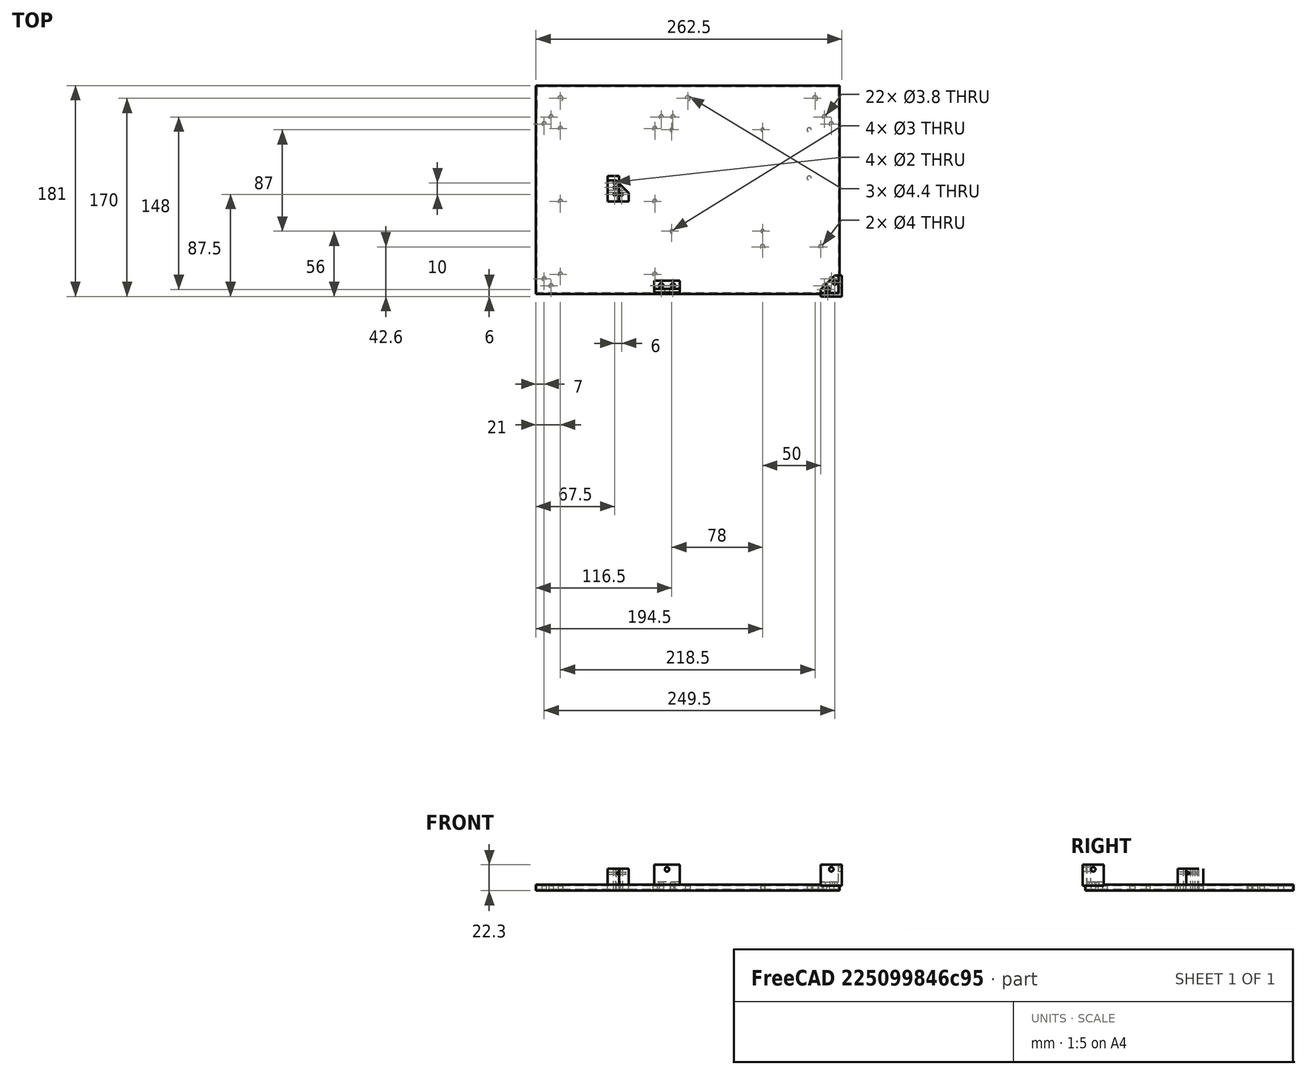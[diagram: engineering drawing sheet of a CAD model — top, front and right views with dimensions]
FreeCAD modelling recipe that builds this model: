
FCSTD DOCUMENT  (FreeCAD 0.18.4R)
Label: bottom_plate
License: All rights reserved
LicenseURL: http://en.wikipedia.org/wiki/All_rights_reserved
objects: Path::FeaturePython×8, Sketcher::SketchObject×6, PartDesign::Pad×6, PartDesign::Body×5, Part::Cylinder×5, Mesh::Feature×4, Part::Part2DObjectPython×4, Part::FeaturePython×4, Part::Box×3, PartDesign::FeatureBase×2, Part::MultiFuse×2, Part::Cut×2, App::Part×2, Spreadsheet::Sheet×1, App::FeaturePython×1, App::DocumentObjectGroup×1, Path::FeatureCompoundPython×1
note: 47 computed .brp shape members not serialized (recipe doc carries the construction recipe); baked Part::Feature solids carry a one-line shape summary decoded from their .brp

FEATURE [Sketcher::SketchObject] Sketch
  MapMode = 5
  Support = -> [XY_Plane]
  expr: Constraints[69] = p.bracket_hole_edge_dist
  expr: Constraints[20] = p.cisco_hole_dist_x
  expr: Constraints[63] = p.bracket_hole_edge_dist
  expr: Constraints[66] = p.bracket_hole_edge_dist
  expr: Constraints[21] = p.cisco_hole_dist_y / 2
  expr: Constraints[51] = p.bracket_hole_edge_dist
  expr: Constraints[54] = p.bracket_hole_dist
  expr: Constraints[13] = p.cisco_hole_dist_y
  expr: Constraints[78] = p.bracket_hole
  expr: Constraints[74] = p.bracket_hole_edge_dist
  expr: Constraints[67] = p.bracket_hole_edge_dist
  expr: Constraints[80] = p.bracket_hole_edge_dist
  expr: Constraints[19] = p.cisco_hole_dist_x
  expr: Constraints[50] = p.bracket_hole_edge_dist
  expr: Constraints[68] = p.bracket_hole_edge_dist
  expr: Constraints[73] = p.bracket_hole_edge_dist
  expr: Constraints[84] = p.bracket_hole_dist
  expr: Constraints[76] = p.bracket_hole_edge_dist
  expr: Constraints[64] = p.bracket_hole_edge_dist
  expr: Constraints[72] = p.bracket_hole_edge_dist
  expr: Constraints[75] = p.bracket_hole_edge_dist
  sketch-geometry (35):
    g0: LineSegment StartX=-78.5 StartY=198 StartZ=0 EndX=78.5 EndY=198 EndZ=0
    g1: LineSegment StartX=78.5 StartY=198 StartZ=0 EndX=78.5 EndY=-60.5 EndZ=0
    g2: LineSegment StartX=78.5 StartY=-60.5 StartZ=0 EndX=-78.5 EndY=-60.5 EndZ=0
    g3: Circle CenterX=-62.5 CenterY=-40.5 CenterZ=0 NormalX=0 NormalY=0 NormalZ=1 AngleXU=0 Radius=1.9
    g4: Circle CenterX=0 CenterY=-40.5 CenterZ=0 NormalX=0 NormalY=0 NormalZ=1 AngleXU=0 Radius=1.9
    g5: Circle CenterX=62.5 CenterY=-40.5 CenterZ=0 NormalX=0 NormalY=0 NormalZ=1 AngleXU=0 Radius=1.9
    g6: Circle CenterX=-62.5 CenterY=40.5 CenterZ=0 NormalX=0 NormalY=0 NormalZ=1 AngleXU=0 Radius=1.9
    g7: Circle CenterX=0 CenterY=40.5 CenterZ=0 NormalX=0 NormalY=0 NormalZ=1 AngleXU=0 Radius=1.9
    g8: Circle CenterX=62.5 CenterY=40.5 CenterZ=0 NormalX=0 NormalY=0 NormalZ=1 AngleXU=0 Radius=1.9
    g9: Circle CenterX=-20.1 CenterY=173 CenterZ=0 NormalX=0 NormalY=0 NormalZ=1 AngleXU=0 Radius=1.8
    g10: Circle CenterX=-61.5 CenterY=173 CenterZ=0 NormalX=0 NormalY=0 NormalZ=1 AngleXU=0 Radius=1.8
    g11: Circle CenterX=-61.5 CenterY=133 CenterZ=0 NormalX=0 NormalY=0 NormalZ=1 AngleXU=0 Radius=1.5
    g12: Circle CenterX=-61.5 CenterY=55 CenterZ=0 NormalX=0 NormalY=0 NormalZ=1 AngleXU=0 Radius=1.5
    g13: Circle CenterX=25.5 CenterY=55 CenterZ=0 NormalX=0 NormalY=0 NormalZ=1 AngleXU=0 Radius=1.5
    g14: Circle CenterX=25.5 CenterY=133 CenterZ=0 NormalX=0 NormalY=0 NormalZ=1 AngleXU=0 Radius=1.5
    g15: Circle CenterX=38.9 CenterY=133 CenterZ=0 NormalX=0 NormalY=0 NormalZ=1 AngleXU=0 Radius=2
    g16: Circle CenterX=38.9 CenterY=183 CenterZ=0 NormalX=0 NormalY=0 NormalZ=1 AngleXU=0 Radius=2
    g17: Circle CenterX=-66.5 CenterY=192 CenterZ=0 NormalX=0 NormalY=0 NormalZ=1 AngleXU=0 Radius=1.9
    g18: Circle CenterX=-72.5 CenterY=186 CenterZ=0 NormalX=0 NormalY=0 NormalZ=1 AngleXU=0 Radius=1.9
    g19: Circle CenterX=66.5 CenterY=192 CenterZ=0 NormalX=0 NormalY=0 NormalZ=1 AngleXU=0 Radius=1.9
    g20: Circle CenterX=72.5 CenterY=186 CenterZ=0 NormalX=0 NormalY=0 NormalZ=1 AngleXU=0 Radius=1.9
    g21: Circle CenterX=72.5 CenterY=46 CenterZ=0 NormalX=0 NormalY=0 NormalZ=1 AngleXU=0 Radius=1.9
    g22: Circle CenterX=72.5 CenterY=-48.5 CenterZ=0 NormalX=0 NormalY=0 NormalZ=1 AngleXU=0 Radius=1.9
    g23: Circle CenterX=66.5 CenterY=-54.5 CenterZ=0 NormalX=0 NormalY=0 NormalZ=1 AngleXU=0 Radius=1.9
    g24: Circle CenterX=-66.5 CenterY=-54.5 CenterZ=0 NormalX=0 NormalY=0 NormalZ=1 AngleXU=0 Radius=1.9
    g25: Circle CenterX=-72.5 CenterY=-48.5 CenterZ=0 NormalX=0 NormalY=0 NormalZ=1 AngleXU=0 Radius=1.9
    g26: Circle CenterX=-72.5 CenterY=56 CenterZ=0 NormalX=0 NormalY=0 NormalZ=1 AngleXU=0 Radius=1.9
    g27: Circle CenterX=-72.5 CenterY=46 CenterZ=0 NormalX=0 NormalY=0 NormalZ=1 AngleXU=0 Radius=1.9
    g28: Circle CenterX=72.5 CenterY=56 CenterZ=0 NormalX=0 NormalY=0 NormalZ=1 AngleXU=0 Radius=1.9
    g29: LineSegment StartX=-78.5 StartY=198 StartZ=0 EndX=-98.5 EndY=198 EndZ=0
    g30: LineSegment StartX=-98.5 StartY=198 StartZ=0 EndX=-98.5 EndY=-60.5 EndZ=0
    g31: LineSegment StartX=-98.5 StartY=-60.5 StartZ=0 EndX=-78.5 EndY=-60.5 EndZ=0
    g32: Circle CenterX=-88.5 CenterY=178 CenterZ=0 NormalX=0 NormalY=0 NormalZ=1 AngleXU=0 Radius=2.2
    g33: Circle CenterX=-88.5 CenterY=68.75 CenterZ=0 NormalX=0 NormalY=0 NormalZ=1 AngleXU=0 Radius=2.2
    g34: Circle CenterX=-88.5 CenterY=-40.5 CenterZ=0 NormalX=0 NormalY=0 NormalZ=1 AngleXU=0 Radius=2.2
  constraints (105):
    c: Coincident(g0,g1)
    c: Coincident(g1,g2)
    c: Horizontal(g0)
    c: Horizontal(g2)
    c: Vertical(g1)
    c: PointOnObject(g4,g-2)
    c: PointOnObject(g7,g-2)
    c: Radius(g6) = 1.9
    c: Equal(g8,g7)
    c: Equal(g7,g6)
    c: Equal(g6,g3)
    c: Equal(g3,g4)
    c: Equal(g4,g5)
    c: DistanceY(g3,g6) = 81
    c: DistanceY(g7,g6) = 0
    c: DistanceY(g8,g7) = 0
    c: DistanceY(g3,g4) = 0
    c: DistanceY(g4,g5) = 0
    c: DistanceX(g3,g6) = 0
    c: DistanceX(g6,g7) = 62.5
    c: DistanceX(g7,g8) = 62.5
    c: DistanceY(g-1,g7) = 40.5
    c: DistanceX(g8,g5) = 0
    c: Radius(g10) = 1.8
    c: Equal(g10,g9)
    c: DistanceX(g10,g9) = 41.4
    c: DistanceY(g10,g9) = 0
    c: DistanceX(g11,g14) = 87
    c: DistanceY(g13,g14) = 78
    c: DistanceY(g14,g11) = 0
    c: DistanceX(g14,g13) = 0
    c: DistanceX(g11,g12) = 0
    c: DistanceY(g13,g12) = 0
    c: Radius(g14) = 1.5
    c: Equal(g14,g11)
    c: Equal(g11,g12)
    c: Equal(g12,g13)
    c: DistanceY(g15,g16) = 50
    c: DistanceX(g15,g16) = 0
    c: Radius(g16) = 2
    c: Equal(g16,g15)
    c: DistanceX(g2,g3) = 16
    c: DistanceX(g5,g1) = 16
    c: DistanceY(g2,g3) = 20
    c: DistanceY(g6,g12) = 14.5
    c: DistanceX(g6,g12) = 1
    c: DistanceY(g14,g15) = 0
    c: DistanceX(g14,g15) = 13.4
    c: DistanceX(g11,g10) = 0
    c: DistanceY(g16,g0) = 15
    c: DistanceY(g17,g0) = 6
    c: DistanceX(g0,g18) = 6
    c: DistanceX(g26,g18) = 0
    c: DistanceX(g27,g26) = 0
    c: DistanceY(g27,g26) = 10
    c: DistanceX(g25,g27) = 0
    c: Equal(g26,g27)
    c: Equal(g27,g25)
    c: Equal(g24,g23)
    c: Equal(g22,g21)
    c: DistanceX(g21,g22) = 0
    c: DistanceY(g26,g18) = 130
    c: DistanceY(g19,g17) = 0
    c: DistanceY(g2,g24) = 6
    c: DistanceX(g25,g24) = 6
    c: Equal(g25,g24)
    c: DistanceY(g24,g25) = 6
    c: DistanceY(g1,g23) = 6
    c: DistanceY(g23,g22) = 6
    c: DistanceX(g23,g22) = 6
    c: Equal(g22,g23)
    c: Equal(g19,g20)
    c: DistanceX(g19,g20) = 6
    c: DistanceY(g20,g19) = 6
    c: DistanceX(g18,g17) = 6
    c: DistanceY(g18,g17) = 6
    c: DistanceX(g20,g0) = 6
    c: Equal(g18,g17)
    c: Radius(g17) = 1.9
    c: Equal(g19,g17)
    c: DistanceX(g22,g1) = 6
    c: DistanceY(g27,g21) = 0
    c: Equal(g21,g28)
    c: DistanceX(g28,g21) = 0
    c: DistanceY(g21,g28) = 10
    c: Equal(g26,g18)
    c: DistanceY(g11,g10) = 40
    c: Coincident(g29,g0)
    c: Horizontal(g29)
    c: Coincident(g30,g29)
    c: Vertical(g30)
    c: Coincident(g31,g30)
    c: Coincident(g31,g2)
    c: Horizontal(g31)
    c: DistanceX(g29,g29) = 20
    c: Radius(g32) = 2.2
    c: Equal(g32,g33)
    c: Equal(g33,g34)
    c: DistanceY(g32,g0) = 20
    c: DistanceY(g2,g34) = 20
    c: DistanceX(g34,g2) = 10
    c: DistanceX(g33,g34) = 0
    c: DistanceX(g33,g32) = 0
    c: DistanceY(g33,g32) = 109.25
    c: DistanceX(g0,g0) = 157
FEATURE [Mesh::Feature] cisco_341_0208  label="cisco_341-0208"
  Placement = pos=(0,0,3) rot=(0,0,1;1.5708rad)
FEATURE [Spreadsheet::Sheet] Spreadsheet  label="p"
  cells = A1=cisco_hole_dist_x; B1(cisco_hole_dist_x)=62.5; A2=cisco_hole_dist_y; B2(cisco_hole_dist_y)=81; A3=bracket_hole_edge_dist; B3(bracket_hole_edge_dist)=6; A4=bracket_wall; B4(bracket_wall)=3; A5=bracket_height; B5(bracket_height)=18; A6=bracket_hole; B6(bracket_hole)=1.9; A7=bracket_hole_dist; B7(bracket_hole_dist)=10; A8=stock_sz_z; B8(stock_sz_z)=3.3; A9=box_sz_z; B9(box_sz_z)=100
FEATURE [PartDesign::Pad] Pad
  Length = 3.3
  Length2 = 100
  Profile = -> Sketch
  Type = 0
  expr: Length = p.stock_sz_z
FEATURE [Part::Part2DObjectPython] ShapeString  label="Cisco PU"  # Draft 2D object (typed FeaturePython)
  AttachmentOffset = pos=(-53,0,0) rot=(0,0,1;0rad)
  FontFile = <path>
  Placement = pos=(-53,0,3.3) rot=(0,0,1;0rad)
  Size = 10
  String = Cisco Power Unit
  Support = -> [Pad]
  Tracking = 0
FEATURE [Mesh::Feature] boxBottom  label="shield bottom"
  Placement = pos=(93,18,3) rot=(0,0,1;0rad)
FEATURE [Mesh::Feature] bottom  label="mosfet_bottom"
  Placement = pos=(158,-29,3) rot=(0,0,1;1.5708rad)
FEATURE [Mesh::Feature] try_me
  Placement = pos=(173,41,3) rot=(0,0,1;1.5708rad)
FEATURE [Part::Part2DObjectPython] ShapeString001  label="Shield"  # Draft 2D object (typed FeaturePython)
  AttachmentOffset = pos=(-38,89,0) rot=(0,0,1;0rad)
  FontFile = <path>
  Placement = pos=(-38,89,3.3) rot=(0,0,1;0rad)
  Size = 10
  String = Shield
  Support = -> [Pad]
  Tracking = 0
FEATURE [Part::Part2DObjectPython] ShapeString002  label="Try Me"  # Draft 2D object (typed FeaturePython)
  AttachmentOffset = pos=(-45,149,0) rot=(0,0,1;0rad)
  FontFile = <path>
  Placement = pos=(-45,149,3.3) rot=(0,0,1;0rad)
  Size = 7
  String = Try Me
  Support = -> [Pad]
  Tracking = 0
FEATURE [Part::Part2DObjectPython] ShapeString003  label="Mosfet"  # Draft 2D object (typed FeaturePython)
  AttachmentOffset = pos=(23,157,0) rot=(0,0,1;0rad)
  FontFile = <path>
  Placement = pos=(23,157,3.3) rot=(0,0,1;0rad)
  Size = 7
  String = Mosfet
  Support = -> [Pad]
  Tracking = 0
FEATURE [PartDesign::Body] Body  label="plate"
  Group = -> [Sketch,Pad,ShapeString,ShapeString001,ShapeString002,ShapeString003]
  Origin = -> Origin
  Placement = pos=(0,0,0) rot=(0,0,-1;1.5708rad)
  Tip = -> Pad
FEATURE [App::FeaturePython] SetupSheet  # Path/CAM operation (typed FeaturePython)
  ClearanceHeightExpression = OpStockZMax+SetupSheet.ClearanceHeightOffset
  ClearanceHeightOffset = 3
  FinalDepthExpression = OpFinalDepth
  HorizRapid = 100
  SafeHeightExpression = OpStockZMax+SetupSheet.SafeHeightOffset
  SafeHeightOffset = 2
  StartDepthExpression = OpStartDepth
  StepDownExpression = OpToolDiameter
  VertRapid = 100
FEATURE [Path::FeaturePython] T4__endmill_2mm  label="T4: endmill 2mm"  # Path/CAM operation (typed FeaturePython)
  HorizFeed = 0
  HorizRapid = 100
  SpindleDir = 0
  SpindleSpeed = 1000
  ToolNumber = 4
  VertFeed = 1
  VertRapid = 100
  expr: HorizRapid = SetupSheet.HorizRapid
  expr: VertRapid = SetupSheet.VertRapid
FEATURE [Path::FeaturePython] T2__drill_3  label="T2: drill 3"  # Path/CAM operation (typed FeaturePython)
  HorizFeed = 1
  HorizRapid = 100
  SpindleDir = 0
  SpindleSpeed = 1000
  ToolNumber = 2
  VertFeed = 1
  VertRapid = 100
  expr: HorizRapid = SetupSheet.HorizRapid
  expr: VertRapid = SetupSheet.VertRapid
FEATURE [Part::FeaturePython] Clone  label="Model-plate"  # Draft clone (typed FeaturePython)
  AttacherType = Attacher::AttachEngine3D
  Fuse = false
  Objects = -> [Body]
  PathResource = Model
  Placement = pos=(0,0,0) rot=(0,0,-1;1.5708rad)
  Scale = (1,1,1)
FEATURE [App::DocumentObjectGroup] Model
  Group = -> [Clone]
FEATURE [Path::FeaturePython] Contour  # Path/CAM operation (typed FeaturePython)
  Active = false
  AreaParams:
    Tolerance = 1e-07
    FitArcs = True
    Simplify = False
    CleanDistance = 0.0
    Accuracy = 0.01
    Unit = 1.0
    MinArcPoints = 4
    MaxArcPoints = 100
    ClipperScale = 10000000.0
    Fill = 0
    Coplanar = 2
    Reorient = True
    Outline = False
    Explode = False
    OpenMode = 0
    Deflection = 0.01
    SubjectFill = 0
    ClipFill = 0
    Offset = 1.0
    ExtraPass = 0
    Stepover = 0.0
    LastStepover = 0.0
    JoinType = 1
    EndType = 0
    MiterLimit = 2.0
    RoundPrecision = 0.0
    PocketMode = 0
    ToolRadius = 1.0
    PocketExtraOffset = 0.0
    PocketStepover = 0.0
    PocketLastStepover = 0.0
    FromCenter = False
    Angle = 45.0
    AngleShift = 0.0
    Shift = 0.0
    Thicken = False
    SectionCount = -1
    Stepdown = 1.0
    SectionOffset = 0.0
    SectionTolerance = 1e-06
    SectionMode = 2
    Project = False
  ClearanceHeight = 5
  Direction = 0
  FinalDepth = -1
  JoinType = 1
  MiterLimit = 0.1
  OffsetExtra = 0
  OpFinalDepth = -1
  OpStartDepth = 4.3
  OpStockZMax = 4.3
  OpStockZMin = -1
  OpToolDiameter = 2
  PathParams = {'orientation': 1, 'feedrate': 0.0, 'feedrate_v': 1.0, 'verbose': True, 'resume_height': 5.0, 'retraction': 5.0, 'return_end': True, 'preamble': False}
  SafeHeight = 5
  Side = 0
  StartDepth = -1
  StartPoint = (0,0,0)
  StepDown = 2
  ToolController = -> T4__endmill_2mm
  UseComp = true
  UseStartPoint = false
FEATURE [Part::FeaturePython] Stock  # WARN: FeaturePython — macro-defined, semantics opaque (R4)
  Base = -> Model
  ExtXneg = 1
  ExtXpos = 1
  ExtYneg = 1
  ExtYpos = 1
  ExtZneg = 1
  ExtZpos = 1
  Placement = pos=(-60.5,-78.5,0) rot=(0,0,1;0rad)
  StockType = FromBase
FEATURE [Path::FeaturePython] Drilling  # Path/CAM operation (typed FeaturePython)
  Active = false
  AddTipLength = false
  Base = -> [Clone]
  ClearanceHeight = 104
  DwellEnabled = false
  DwellTime = 0
  FinalDepth = 3.3
  OpFinalDepth = 3.3
  OpStartDepth = 101
  OpStockZMax = 101
  OpStockZMin = -1
  OpToolDiameter = 3
  PeckDepth = 0
  PeckEnabled = false
  RetractHeight = 10
  ReturnLevel = 0
  SafeHeight = 103
  StartDepth = 4
  ToolController = -> T2__drill_3
  expr: ClearanceHeight = OpStockZMax + SetupSheet.ClearanceHeightOffset
  expr: SafeHeight = OpStockZMax + SetupSheet.SafeHeightOffset
  expr: FinalDepth = OpFinalDepth
FEATURE [Sketcher::SketchObject] Sketch009  label="angular003"
  expr: Constraints[19] = p.bracket_hole_edge_dist
  expr: Constraints[18] = p.bracket_hole_edge_dist
  expr: Constraints[13] = p.bracket_hole
  expr: Constraints[20] = p.bracket_hole_edge_dist
  expr: Constraints[15] = p.bracket_hole_edge_dist
  expr: Constraints[12] = p.bracket_hole_edge_dist
  expr: Constraints[11] = p.bracket_hole_edge_dist
  sketch-geometry (7):
    g0: LineSegment StartX=0 StartY=-18 StartZ=0 EndX=0 EndY=0 EndZ=0
    g1: LineSegment StartX=0 StartY=0 StartZ=0 EndX=18 EndY=0 EndZ=0
    g2: LineSegment StartX=18 StartY=0 StartZ=0 EndX=18 EndY=-6 EndZ=0
    g3: LineSegment StartX=18 StartY=-6 StartZ=0 EndX=6 EndY=-18 EndZ=0
    g4: LineSegment StartX=6 StartY=-18 StartZ=0 EndX=0 EndY=-18 EndZ=0
    g5: Circle CenterX=6 CenterY=-12 CenterZ=0 NormalX=0 NormalY=0 NormalZ=1 AngleXU=0 Radius=1.9
    g6: Circle CenterX=12 CenterY=-6 CenterZ=0 NormalX=0 NormalY=0 NormalZ=1 AngleXU=0 Radius=1.9
  constraints (21):
    c: Vertical(g0)
    c: Coincident(g0,g1)
    c: Coincident(g1,g2)
    c: Coincident(g2,g3)
    c: Coincident(g3,g4)
    c: Coincident(g4,g0)
    c: Horizontal(g1)
    c: Horizontal(g4)
    c: Vertical(g2)
    c: Equal(g2,g4)
    c: Equal(g1,g0)
    c: DistanceX(g6,g1) = 6
    c: DistanceX(g5,g6) = 6
    c: Radius(g5) = 1.9
    c: Equal(g5,g6)
    c: DistanceX(g4,g4) = 6
    c: DistanceX(g-1,g0) = 0
    c: DistanceY(g0,g-1) = 0
    c: DistanceX(g0,g5) = 6
    c: DistanceY(g0,g5) = 6
    c: DistanceY(g5,g6) = 6
FEATURE [PartDesign::Pad] Pad006
  Length = 3
  Length2 = 100
  Profile = -> Sketch009
  Type = 0
FEATURE [Sketcher::SketchObject] Sketch010
  Placement = pos=(3,0,0) rot=(0.57735,-0.57735,-0.57735;2.0944rad)
  Support = -> [Pad006]
  expr: Constraints[10] = p.bracket_height
  expr: Constraints[9] = p.bracket_hole
  sketch-geometry (5):
    g0: LineSegment StartX=0 StartY=0 StartZ=0 EndX=18 EndY=0 EndZ=0
    g1: LineSegment StartX=18 StartY=0 StartZ=0 EndX=18 EndY=18 EndZ=0
    g2: LineSegment StartX=18 StartY=18 StartZ=0 EndX=0 EndY=18 EndZ=0
    g3: LineSegment StartX=0 StartY=18 StartZ=0 EndX=0 EndY=0 EndZ=0
    g4: Circle CenterX=9 CenterY=14 CenterZ=0 NormalX=0 NormalY=0 NormalZ=1 AngleXU=0 Radius=1.9
  constraints (14):
    c: Coincident(g0,g1)
    c: Coincident(g1,g2)
    c: Coincident(g2,g3)
    c: Coincident(g3,g0)
    c: Horizontal(g0)
    c: Horizontal(g2)
    c: Vertical(g1)
    c: Vertical(g3)
    c: Coincident(g0,g-1)
    c: Radius(g4) = 1.9
    c: DistanceY(g3,g3) = 18
    c: DistanceY(g4,g2) = 4
    c: DistanceX(g0,g4) = 9
    c: DistanceX(g0,g0) = 18
FEATURE [Sketcher::SketchObject] Sketch011
  MapMode = 5
  Placement = pos=(0,0,0) rot=(0,0.707107,0.707107;3.14159rad)
  Support = -> [Pad006]
  expr: Constraints[10] = p.bracket_height
  expr: Constraints[9] = p.bracket_hole
  sketch-geometry (5):
    g0: LineSegment StartX=-18 StartY=0 StartZ=0 EndX=0 EndY=0 EndZ=0
    g1: LineSegment StartX=0 StartY=0 StartZ=0 EndX=0 EndY=18 EndZ=0
    g2: LineSegment StartX=0 StartY=18 StartZ=0 EndX=-18 EndY=18 EndZ=0
    g3: LineSegment StartX=-18 StartY=18 StartZ=0 EndX=-18 EndY=0 EndZ=0
    g4: Circle CenterX=-9 CenterY=14 CenterZ=0 NormalX=0 NormalY=0 NormalZ=1 AngleXU=0 Radius=1.9
  constraints (15):
    c: Coincident(g0,g1)
    c: Coincident(g1,g2)
    c: Coincident(g2,g3)
    c: Coincident(g3,g0)
    c: Horizontal(g0)
    c: Horizontal(g2)
    c: Vertical(g1)
    c: Vertical(g3)
    c: DistanceX(g0,g0) = 18
    c: Radius(g4) = 1.9
    c: DistanceY(g3,g3) = 18
    c: DistanceY(g4,g2) = 4
    c: DistanceX(g0,g4) = 9
    c: DistanceX(g0,g-1) = 0
    c: DistanceY(g-1,g0) = 0
FEATURE [PartDesign::Pad] Pad007
  BaseFeature = -> Pad006
  Length = 3
  Length2 = 100
  Profile = -> Sketch010
  Type = 0
  expr: Length = p.bracket_wall
FEATURE [PartDesign::Pad] Pad008
  BaseFeature = -> Pad007
  Length = 3
  Length2 = 100
  Profile = -> Sketch011
  Reversed = true
  Type = 0
  expr: Length = p.bracket_wall
FEATURE [PartDesign::Body] Body005  label="corner bracket"
  Group = -> [Pad006,Sketch009,Sketch010,Sketch011,Pad007,Pad008]
  Origin = -> Origin005
  Placement = pos=(25,0,3.3) rot=(0,0,1;0rad)
  Tip = -> Pad008
  expr: Placement.Base.z = p.stock_sz_z
FEATURE [Sketcher::SketchObject] Sketch012  label="angular004"
  AttachmentOffset = pos=(20,-13,-3) rot=(0,0,1;0rad)
  expr: Constraints[11] = p.bracket_hole_edge_dist
  expr: Constraints[9] = p.bracket_hole_edge_dist
  expr: Constraints[4] = p.bracket_hole_edge_dist
  expr: Constraints[6] = p.bracket_hole
  expr: Constraints[5] = p.bracket_hole_dist
  sketch-geometry (6):
    g0: LineSegment StartX=0 StartY=-10 StartZ=0 EndX=0 EndY=0 EndZ=0
    g1: LineSegment StartX=0 StartY=0 StartZ=0 EndX=22 EndY=0 EndZ=0
    g2: LineSegment StartX=22 StartY=0 StartZ=0 EndX=22 EndY=-10 EndZ=0
    g3: Circle CenterX=6 CenterY=-6 CenterZ=0 NormalX=0 NormalY=0 NormalZ=1 AngleXU=0 Radius=1.9
    g4: Circle CenterX=16 CenterY=-6 CenterZ=0 NormalX=0 NormalY=0 NormalZ=1 AngleXU=0 Radius=1.9
    g5: LineSegment StartX=0 StartY=-10 StartZ=0 EndX=22 EndY=-10 EndZ=0
  constraints (18):
    c: Vertical(g0)
    c: Coincident(g0,g1)
    c: Coincident(g1,g2)
    c: Horizontal(g1)
    c: DistanceX(g4,g1) = 6
    c: DistanceX(g3,g4) = 10
    c: Radius(g3) = 1.9
    c: Equal(g3,g4)
    c: DistanceY(g3,g4) = 0
    c: DistanceY(g3,g0) = 6
    c: DistanceY(g2,g2) = 10
    c: DistanceX(g0,g3) = 6
    c: Equal(g0,g2)
    c: Coincident(g5,g0)
    c: Coincident(g5,g2)
    c: Equal(g5,g1)
    c: DistanceY(g0,g-1) = 0
    c: DistanceX(g-1,g0) = 0
FEATURE [PartDesign::Pad] Pad009
  Length = 3
  Length2 = 100
  Profile = -> Sketch012
  Type = 0
  expr: Length = p.bracket_wall
FEATURE [Sketcher::SketchObject] Sketch013
  MapMode = 5
  Placement = pos=(0,0,0) rot=(1,0,0;1.5708rad)
  Support = -> [Pad009]
  expr: Constraints[12] = p.bracket_hole_edge_dist + p.bracket_hole_dist / 2
  expr: Constraints[8] = p.bracket_hole_edge_dist * 2 + p.bracket_hole_dist
  expr: Constraints[10] = p.bracket_height
  expr: Constraints[9] = p.bracket_hole
  sketch-geometry (5):
    g0: LineSegment StartX=0 StartY=0 StartZ=0 EndX=22 EndY=0 EndZ=0
    g1: LineSegment StartX=22 StartY=0 StartZ=0 EndX=22 EndY=18 EndZ=0
    g2: LineSegment StartX=22 StartY=18 StartZ=0 EndX=0 EndY=18 EndZ=0
    g3: LineSegment StartX=0 StartY=18 StartZ=0 EndX=0 EndY=0 EndZ=0
    g4: Circle CenterX=11 CenterY=14 CenterZ=0 NormalX=0 NormalY=0 NormalZ=1 AngleXU=0 Radius=1.9
  constraints (15):
    c: Coincident(g0,g1)
    c: Coincident(g1,g2)
    c: Coincident(g2,g3)
    c: Coincident(g3,g0)
    c: Horizontal(g0)
    c: Horizontal(g2)
    c: Vertical(g1)
    c: Vertical(g3)
    c: DistanceX(g0,g0) = 22
    c: Radius(g4) = 1.9
    c: DistanceY(g3,g3) = 18
    c: DistanceY(g4,g2) = 4
    c: DistanceX(g0,g4) = 11
    c: DistanceY(g-1,g0) = 0
    c: DistanceX(g-1,g0) = 0
FEATURE [PartDesign::Pad] Pad010
  BaseFeature = -> Pad009
  Length = 3
  Length2 = 100
  Profile = -> Sketch013
  Type = 0
  expr: Length = p.bracket_wall
FEATURE [PartDesign::Body] Body006  label="bracket"
  Group = -> [Sketch013,Sketch012,Pad009,Pad010]
  Origin = -> Origin006
  Placement = pos=(40,79,3.3) rot=(0,0,1;0rad)
  Tip = -> Pad010
  expr: Placement.Base.z = p.stock_sz_z
FEATURE [Path::FeaturePython] T3__laser  label="T3: laser"  # Path/CAM operation (typed FeaturePython)
  HorizFeed = 50
  HorizRapid = 100
  SpindleDir = 0
  SpindleSpeed = 1000
  ToolNumber = 3
  VertFeed = 0.1
  VertRapid = 100
  expr: HorizRapid = SetupSheet.HorizRapid
  expr: VertRapid = SetupSheet.VertRapid
FEATURE [Path::FeaturePython] Engrave  # Path/CAM operation (typed FeaturePython)
  Active = true
  Base = -> [Clone]
  ClearanceHeight = 7.3
  FinalDepth = 0
  OpFinalDepth = 3.2
  OpStartDepth = 3.3
  OpStockZMax = 4.3
  OpStockZMin = -1
  OpToolDiameter = 0.2
  SafeHeight = 6.3
  StartDepth = 0
  StartVertex = 0
  StepDown = 0
  ToolController = -> T3__laser
  expr: ClearanceHeight = OpStockZMax + SetupSheet.ClearanceHeightOffset
  expr: SafeHeight = OpStockZMax + SetupSheet.SafeHeightOffset
FEATURE [Path::FeaturePython] Contour001  # Path/CAM operation (typed FeaturePython)
  Active = true
  AreaParams:
    Tolerance = 1e-07
    FitArcs = True
    Simplify = False
    CleanDistance = 0.0
    Accuracy = 0.01
    Unit = 1.0
    MinArcPoints = 4
    MaxArcPoints = 100
    ClipperScale = 10000000.0
    Fill = 0
    Coplanar = 2
    Reorient = True
    Outline = False
    Explode = False
    OpenMode = 0
    Deflection = 0.01
    SubjectFill = 0
    ClipFill = 0
    Offset = 0.1
    ExtraPass = 0
    Stepover = 0.0
    LastStepover = 0.0
    JoinType = 0
    EndType = 0
    MiterLimit = 2.0
    RoundPrecision = 0.0
    PocketMode = 0
    ToolRadius = 1.0
    PocketExtraOffset = 0.0
    PocketStepover = 0.0
    PocketLastStepover = 0.0
    FromCenter = False
    Angle = 45.0
    AngleShift = 0.0
    Shift = 0.0
    Thicken = False
    SectionCount = -1
    Stepdown = 1.0
    SectionOffset = 0.0
    SectionTolerance = 1e-06
    SectionMode = 2
    Project = False
  ClearanceHeight = 7.3
  Direction = 0
  FinalDepth = 0
  JoinType = 0
  MiterLimit = 0.1
  OffsetExtra = 0
  OpFinalDepth = -1
  OpStartDepth = 4.3
  OpStockZMax = 4.3
  OpStockZMin = -1
  OpToolDiameter = 0.2
  PathParams = {'orientation': 1, 'feedrate': 50.0, 'feedrate_v': 0.1, 'verbose': True, 'resume_height': 6.3, 'retraction': 7.3, 'return_end': True, 'preamble': False}
  SafeHeight = 6.3
  Side = 0
  StartDepth = 0
  StartPoint = (0,0,0)
  StepDown = 0.2
  ToolController = -> T3__laser
  UseComp = true
  UseStartPoint = false
  expr: ClearanceHeight = OpStockZMax + SetupSheet.ClearanceHeightOffset
  expr: SafeHeight = OpStockZMax + SetupSheet.SafeHeightOffset
  expr: StepDown = OpToolDiameter
FEATURE [Path::FeatureCompoundPython] Operations  # Path/CAM operation (typed FeaturePython)
  Group = -> [Drilling,Contour,Engrave,Contour001]
  UsePlacements = false
FEATURE [Path::FeaturePython] Job  # Path/CAM operation (typed FeaturePython)
  GeometryTolerance = 0.01
  Model = -> Model
  Operations = -> Operations
  PostProcessor = 1
  PostProcessorOutputFile = <userpath>/work/roborep/gcode
  SetupSheet = -> SetupSheet
  Stock = -> Stock
  ToolController = -> [T4__endmill_2mm,T2__drill_3,T3__laser]
FEATURE [PartDesign::FeatureBase] Clone001
  BaseFeature = -> Body006
  Placement = pos=(40,79,3.3) rot=(0,0,1;0rad)
FEATURE [PartDesign::Body] Body007  label="bracket clone"
  BaseFeature = -> Body006
  Group = -> [Clone001]
  Origin = -> Origin007
  Placement = pos=(102,1,0) rot=(0,0,1;3.14159rad)
  Tip = -> Clone001
FEATURE [PartDesign::FeatureBase] Clone002
  BaseFeature = -> Body005
  Placement = pos=(25,0,3.3) rot=(0,0,1;0rad)
FEATURE [PartDesign::Body] Body008  label="corner bracket clone 1"
  BaseFeature = -> Body005
  Group = -> [Clone002]
  Origin = -> Origin008
  Placement = pos=(226,-81.5,0) rot=(0,0,1;3.14159rad)
  Tip = -> Clone002
FEATURE [Part::Box] Box  label="Cube"
  AttacherType = Attacher::AttachEngine3D
  Height = 18
  Length = 10
  Width = 22
  expr: Width = p.bracket_hole_edge_dist * 2 + p.bracket_hole_dist
  expr: Height = p.bracket_height
FEATURE [Part::Cylinder] Cylinder
  Angle = 360
  AttacherType = Attacher::AttachEngine3D
  Height = 50
  Placement = pos=(0,0,-10) rot=(0,0,1;0rad)
  Radius = 1
FEATURE [Part::FeaturePython] Array  # Draft array (typed FeaturePython)
  Angle = 360
  ArrayType = 0
  Axis = (0,0,1)
  Base = -> Cylinder
  Center = (0,0,0)
  Fuse = false
  IntervalAxis = (0,0,0)
  IntervalX = (1,0,0)
  IntervalY = (0,10,0)
  IntervalZ = (0,0,1)
  NumberPolar = 1
  NumberX = 1
  NumberY = 2
  NumberZ = 1
  Placement = pos=(6,6,0) rot=(0,0,1;0rad)
  expr: Placement.Base.x = p.bracket_hole_edge_dist
  expr: Placement.Base.y = p.bracket_hole_edge_dist
  expr: IntervalY.y = p.bracket_hole_dist
FEATURE [Part::Cylinder] Cylinder001
  Angle = 360
  AttacherType = Attacher::AttachEngine3D
  Height = 50
  Placement = pos=(-10,11,14) rot=(0,1,0;1.5708rad)
  Radius = 1
  expr: Placement.Base.y = p.bracket_hole_edge_dist + p.bracket_hole_dist / 2
  expr: Placement.Base.z = p.bracket_height - 4
FEATURE [Part::MultiFuse] Fusion
  Shapes = -> [Array,Cylinder001]
FEATURE [Part::Cut] Cut
  Base = -> Box
  Tool = -> Fusion
FEATURE [App::Part] Part  label="side box part"
  Group = -> [Box,Cylinder,Array,Cylinder001,Fusion,Cut]
  Origin = -> Origin009
  Placement = pos=(62,-78,3.3) rot=(0,0,1;1.5708rad)
  expr: Placement.Base.z = p.stock_sz_z
FEATURE [Part::Box] Box001  label="Cube001"
  AttacherType = Attacher::AttachEngine3D
  Height = 18
  Length = 18
  Width = 18
  expr: Height = p.bracket_height
FEATURE [Part::Cylinder] Cylinder002
  Angle = 360
  AttacherType = Attacher::AttachEngine3D
  Height = 50
  Placement = pos=(6,12,-10) rot=(0,0,1;0rad)
  Radius = 1
  expr: Placement.Base.x = p.bracket_hole_edge_dist
  expr: Placement.Base.y = 18 - p.bracket_hole_edge_dist
FEATURE [Part::FeaturePython] Array001  # Draft array (typed FeaturePython)
  Angle = 360
  ArrayType = 0
  Axis = (0,0,1)
  Base = -> Cylinder002
  Center = (0,0,0)
  Fuse = false
  IntervalAxis = (0,0,0)
  IntervalX = (10,10,0)
  IntervalY = (6,-6,0)
  IntervalZ = (0,0,1)
  NumberPolar = 1
  NumberX = 1
  NumberY = 2
  NumberZ = 1
  expr: IntervalY.x = p.bracket_hole_edge_dist
  expr: IntervalX.y = p.bracket_hole_dist
  expr: IntervalY.y = -p.bracket_hole_edge_dist
  expr: IntervalX.x = p.bracket_hole_dist
FEATURE [Part::Cylinder] Cylinder003
  Angle = 360
  AttacherType = Attacher::AttachEngine3D
  Height = 50
  Placement = pos=(-17,9,14) rot=(0,1,0;1.5708rad)
  Radius = 1
  expr: Placement.Base.y = 18 / 2
  expr: Placement.Base.z = p.bracket_height - 4
FEATURE [Part::Cylinder] Cylinder004
  Angle = 360
  AttacherType = Attacher::AttachEngine3D
  Height = 50
  Placement = pos=(9,27,14) rot=(1,0,0;1.5708rad)
  Radius = 1
  expr: Placement.Base.x = 18 / 2
  expr: Placement.Base.z = p.bracket_height - 4
FEATURE [Part::Box] Box002  label="Cube002"
  AttacherType = Attacher::AttachEngine3D
  Height = 18
  Length = 18
  Placement = pos=(28.8715,-3.57359,0) rot=(0,0,1;0.785398rad)
  Width = 50
  expr: Height = p.bracket_height
FEATURE [Part::MultiFuse] Fusion001
  Shapes = -> [Array001,Cylinder003,Cylinder004,Box002]
FEATURE [Part::Cut] Cut001
  Base = -> Box001
  Tool = -> Fusion001
FEATURE [App::Part] Part001  label="corner box part"
  Group = -> [Box001,Cylinder002,Array001,Cylinder003,Cylinder004,Fusion001,Cut001,Box002]
  Origin = -> Origin010
  Placement = pos=(201,-81.5,3.3) rot=(0,0,1;1.5708rad)
  expr: Placement.Base.z = p.stock_sz_z
note: 4 file-system paths scrubbed to <path> (originals preserved in the JSON sidecar)
